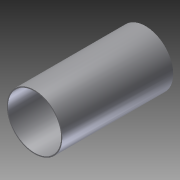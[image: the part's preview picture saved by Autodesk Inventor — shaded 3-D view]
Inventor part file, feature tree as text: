
AUTODESK INVENTOR PART (.ipt)
format: ipt  version: 2012 (Build 160160000, 160)  size: 83,968 bytes
history: native  units: in
note: dims shown in document units (in); Inventor stores cm internally (conversion verified against a paired STEP export)
features: extrude x1, shell x1, sketch x1
ambient origin geometry x8: Origin, YZ Plane, XZ Plane, XY Plane, X Axis, Y Axis, Z Axis, Center Point
bodies: Solid1 (feature_tree)
feature tree (3):
  extrude  "Extrusion1"  Depth=10.0in TaperAngle=0.0deg
  shell  "Shell1"  Thickness=0.1in
  sketch  "Sketch1"  dims[d0=5.0in d1=10.0in d2=0.0in d3=0.1in]
